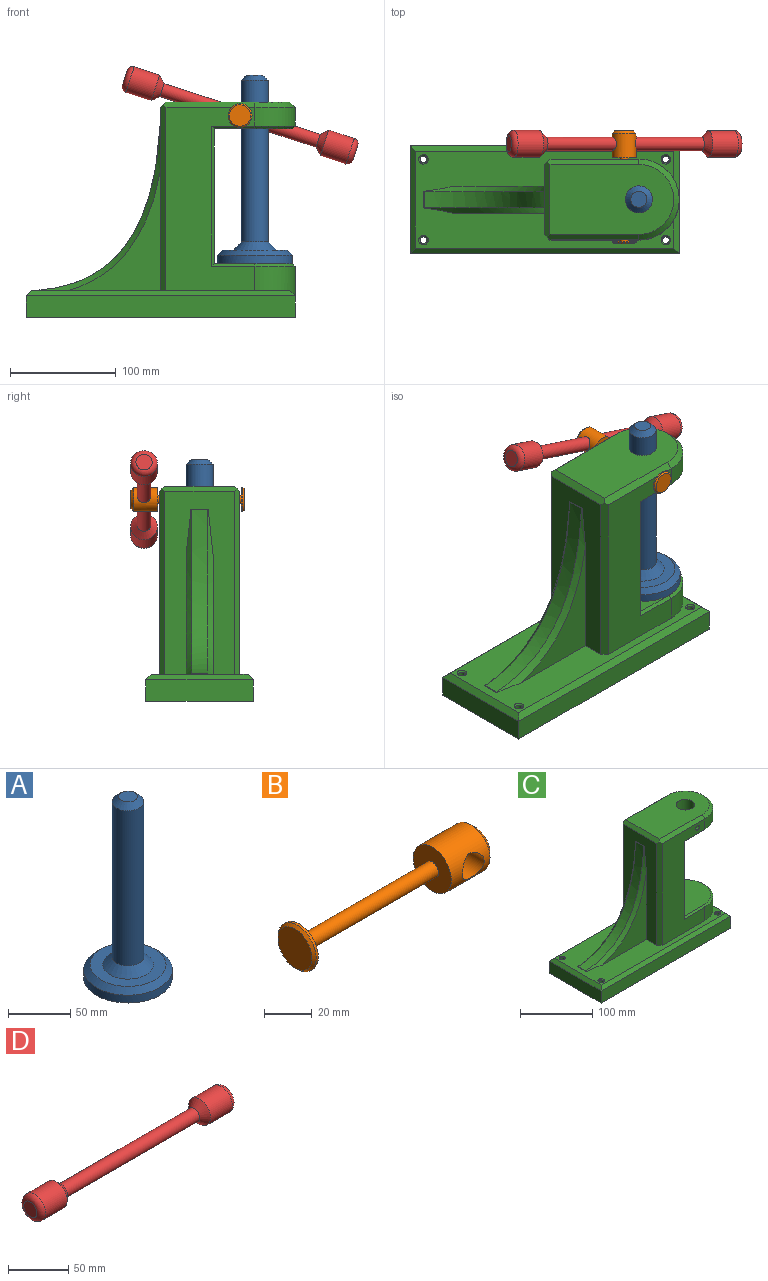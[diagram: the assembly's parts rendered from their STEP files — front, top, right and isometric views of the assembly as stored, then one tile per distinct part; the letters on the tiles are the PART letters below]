
ASSEMBLY  parts=4 mates=3
PART A: 8 faces, bbox 71.1x71.1x177.8 mm
  f0: plane 15.24x15.24mm, normal (0,0,1), area 182.4mm2, adj f6
  f1: plane 71.12x71.12mm, normal (0,0,-1), area 3972.6mm2, adj f2
  f2: cylinder r=35.56mm len=71.12mm, axis (0,0,1), area 1702.5mm2, adj f1,f5
  f3: plane 60.96x60.96mm, normal (0,0,1), area 1621.5mm2, adj f5,f7
  f4: cylinder r=12.7mm len=152.4mm, axis (0,0,1), area 12161mm2, adj f6,f7
  f5: cone r=30.48mm half-angle=45deg, axis (0,0,-1), area 1490.5mm2, adj f2,f3
  f6: cone r=7.62mm half-angle=45deg, axis (0,0,-1), area 458.6mm2, adj f0,f4
  f7: cone r=12.7mm half-angle=45deg, axis (0,0,-1), area 1117.9mm2, adj f3,f4
PART B: 10 faces, bbox 106.7x22.6x22.6 mm
  f0: plane 20.07x20.07mm, normal (-1,0,0), area 316.2mm2, adj f9
  f1: cylinder r=11.3mm len=22.61mm, axis (-1,0,0), area 90.2mm2, adj f2,f9
  f2: plane 22.61x22.61mm, normal (1,0,0), area 358.7mm2, adj f1,f3
  f3: cylinder r=3.68mm len=78.74mm, axis (-1,0,0), area 1822.1mm2, adj f2,f4
  f4: plane 22.61x22.61mm, normal (-1,0,0), area 358.7mm2, adj f3,f5
  f5: cylinder r=11.3mm len=22.86mm, axis (-1,0,0), area 1358.9mm2, adj f4,f7,f8
  f6: plane 17.53x17.53mm, normal (1,0,0), area 241.2mm2, adj f8
  f7: cylinder r=6.35mm len=22.61mm, axis (0,-1,0), area 825.9mm2, adj f5
  f8: cone r=11.3mm half-angle=45deg, axis (-1,0,0), area 226.4mm2, adj f5,f6
  f9: cone r=10.03mm half-angle=45deg, axis (1,0,0), area 120.4mm2, adj f0,f1
PART C: 51 faces, bbox 256.5x104.1x205.7 mm
  f0: plane 243.84x91.44mm, normal (0,0,1), area 10405.7mm2, adj f7,f12,f13,f14,f15,f16,f18,f19
  f1: plane 101.6x20.32mm, normal (-1,0,0), area 2064.5mm2, adj f2,f4,f5,f13
  f2: plane 254x101.6mm, normal (0,0,-1), area 25679.7mm2, adj f1,f3,f4,f5,f8,f9,f10,f11
  f3: plane 101.6x20.32mm, normal (1,0,0), area 2064.5mm2, adj f2,f4,f5,f14,f16
  f4: plane 254x20.32mm, normal (0,-1,0), area 5161.3mm2, adj f1,f2,f3,f12
  f5: plane 254x20.32mm, normal (0,1,0), area 5161.3mm2, adj f1,f2,f3,f15
  f6: plane 73.66x71.12mm, normal (0,0,1), area 4696mm2, adj f17,f29,f32,f33
  f7: cylinder r=38.1mm len=76.2mm, axis (0,0,1), area 2837.3mm2, adj f0,f14,f16,f17,f30,f31
  f8: cylinder r=3.17mm len=24.13mm, axis (0,0,1), area 481.4mm2, adj f2,f19
  f9: cylinder r=3.17mm len=24.13mm, axis (0,0,1), area 481.4mm2, adj f2,f20
  f10: cylinder r=3.17mm len=24.13mm, axis (0,0,1), area 481.4mm2, adj f2,f21
  f11: cylinder r=3.17mm len=24.13mm, axis (0,0,1), area 481.4mm2, adj f2,f18
  f12: plane 254x5.08mm, normal (0,-0.71,0.71), area 1788.3mm2, adj f0,f4,f13,f14
  f13: plane 101.6x5.08mm, normal (-0.71,0,0.71), area 693.4mm2, adj f0,f1,f12,f15
  f14: plane 53.3x7.58mm, normal (0.71,0,0.71), area 254.4mm2, adj f0,f3,f7,f12
  f15: plane 254x5.08mm, normal (0,0.71,0.71), area 1788.3mm2, adj f0,f5,f13,f16
  f16: plane 53.3x7.58mm, normal (0.71,0,0.71), area 254.4mm2, adj f0,f3,f7,f15
  f17: cone r=35.56mm half-angle=45deg, axis (0,0,-1), area 415.6mm2, adj f6,f7,f32,f33
  f18: cone r=3.17mm half-angle=45deg, axis (0,0,1), area 43mm2, adj f0,f11
  f19: cone r=3.17mm half-angle=45deg, axis (0,0,1), area 43mm2, adj f0,f8
  f20: cone r=3.17mm half-angle=45deg, axis (0,0,1), area 43mm2, adj f0,f9
  f21: cone r=3.17mm half-angle=45deg, axis (0,0,1), area 43mm2, adj f0,f10
  f22: plane 73.66x71.12mm, normal (0,0,-1), area 4189.3mm2, adj f25,f27,f29,f34,f35
  f23: plane 116.84x66.04mm, normal (0,0,1), area 6741.4mm2, adj f26,f27,f38,f40,f42
  f24: cylinder r=38.1mm len=76.2mm, axis (0,0,1), area 2128.2mm2, adj f25,f26,f30,f31
  f25: cone r=38.1mm half-angle=45deg, axis (0,0,1), area 415.6mm2, adj f22,f24,f34,f35
  f26: cone r=33.02mm half-angle=45deg, axis (0,0,-1), area 802.6mm2, adj f23,f24,f38,f40
  f27: cylinder r=12.7mm len=25.4mm, axis (0,0,1), area 1929.3mm2, adj f22,f23,f43
  f28: plane 172.72x66.04mm, normal (-1,0,0), area 7677.6mm2, adj f0,f39,f41,f42,f45,f46,f48,f49
  f29: plane 127x71.12mm, normal (1,0,0), area 9032.2mm2, adj f6,f22,f36,f37
  f30: plane 172.72x83.82mm, normal (0,-1,0), area 9064.1mm2, adj f0,f7,f24,f33,f34,f37,f40,f41
  f31: plane 172.72x83.82mm, normal (0,1,0), area 9064.1mm2, adj f0,f7,f24,f32,f35,f36,f38,f39
  f32: plane 40.64x2.54mm, normal (0,0.71,0.71), area 141.4mm2, adj f6,f17,f31,f36
  f33: plane 40.64x2.54mm, normal (0,-0.71,0.71), area 141.4mm2, adj f6,f17,f30,f37
  f34: plane 40.64x2.54mm, normal (0,-0.71,-0.71), area 141.4mm2, adj f22,f25,f30,f37
  f35: plane 40.64x2.54mm, normal (0,0.71,-0.71), area 141.4mm2, adj f22,f25,f31,f36
  f36: plane 132.08x2.54mm, normal (0.71,0.71,0), area 465.3mm2, adj f29,f31,f32,f35
  f37: plane 132.08x2.54mm, normal (0.71,-0.71,0), area 465.3mm2, adj f29,f30,f33,f34
  f38: plane 86.36x5.08mm, normal (0,0.71,0.71), area 611.3mm2, adj f23,f26,f31,f39,f42
  f39: plane 175.26x5.08mm, normal (-0.71,0.71,0), area 1250mm2, adj f0,f28,f31,f38,f42
  f40: plane 86.36x5.08mm, normal (0,-0.71,0.71), area 611.3mm2, adj f23,f26,f30,f41,f42
  f41: plane 175.26x5.08mm, normal (-0.71,-0.71,0), area 1250mm2, adj f0,f28,f30,f40,f42
  f42: plane 71.12x5.08mm, normal (-0.71,0,0.71), area 492.7mm2, adj f23,f28,f38,f39,f40,f41
  f43: cylinder r=3.81mm len=76.2mm, axis (0,-1,0), area 1712.1mm2, adj f27,f30,f31
  f44: extruded ~155.52x113.29mm, area 3257.3mm2, adj f47,f48,f49,f50
  f45: plane 113.35x86.99mm, normal (0,-1,0), area 2844.3mm2, adj f0,f28,f48
  f46: plane 113.35x86.99mm, normal (0,1,0), area 2844.3mm2, adj f0,f28,f49
  f47: plane 16.26x0.51mm, normal (-1,0,-0.04), area 8mm2, adj f0,f44,f48,f49
  f48: bspline ~167.43x130.49mm, area 1294.4mm2, adj f0,f28,f44,f45,f47,f50
  f49: bspline ~167.43x130.49mm, area 1294.4mm2, adj f0,f28,f44,f46,f47,f50
  f50: plane 16.26x0.51mm, normal (0.02,0,1), area 8mm2, adj f28,f44,f48,f49
PART D: 9 faces, bbox 228.6x27.5x27.5 mm
  f0: cylinder r=6.35mm len=154.94mm, axis (1,0,0), area 6181.8mm2, adj f7,f8
  f1: cylinder r=12.7mm len=25.4mm, axis (1,0,0), area 2026.8mm2, adj f5,f8
  f2: plane 15.24x15.24mm, normal (-1,0,0), area 182.4mm2, adj f5
  f3: plane 15.24x15.24mm, normal (1,0,0), area 182.4mm2, adj f6
  f4: cylinder r=12.7mm len=25.4mm, axis (1,0,0), area 2026.8mm2, adj f6,f7
  f5: torus R=7.62mm, axis (1,0,0), area 544.2mm2, adj f1,f2
  f6: torus R=7.62mm, axis (1,0,0), area 544.2mm2, adj f3,f4
  f7: cone r=12.7mm half-angle=45deg, axis (1,0,0), area 537.4mm2, adj f0,f4
  f8: cone r=5.08mm half-angle=45deg, axis (-1,0,0), area 537.4mm2, adj f0,f1
PLACE A t=(30.53,0,93.6)mm
PLACE B rot(axis=(0.15,0.15,0.98),91.4deg) t=(-8.76,39.37,225.86)mm
PLACE C t=(-82.55,0,51.56)mm fixed
PLACE D rot(axis=(0,-1,0),162deg) t=(-80.09,52.42,252.91)mm
MATE cylindrical D.f0 <-> B.f7  axis (-0.95,0,0.31) through (-7.62,52.42,229.36)mm
MATE revolute B.f9 <-> C.f43  axis (0,-1,0) through (-7.62,0,229.36)mm
MATE slider A.f7 <-> C.f27  axis (0,0,1) through (6.35,0,186.18)mm
